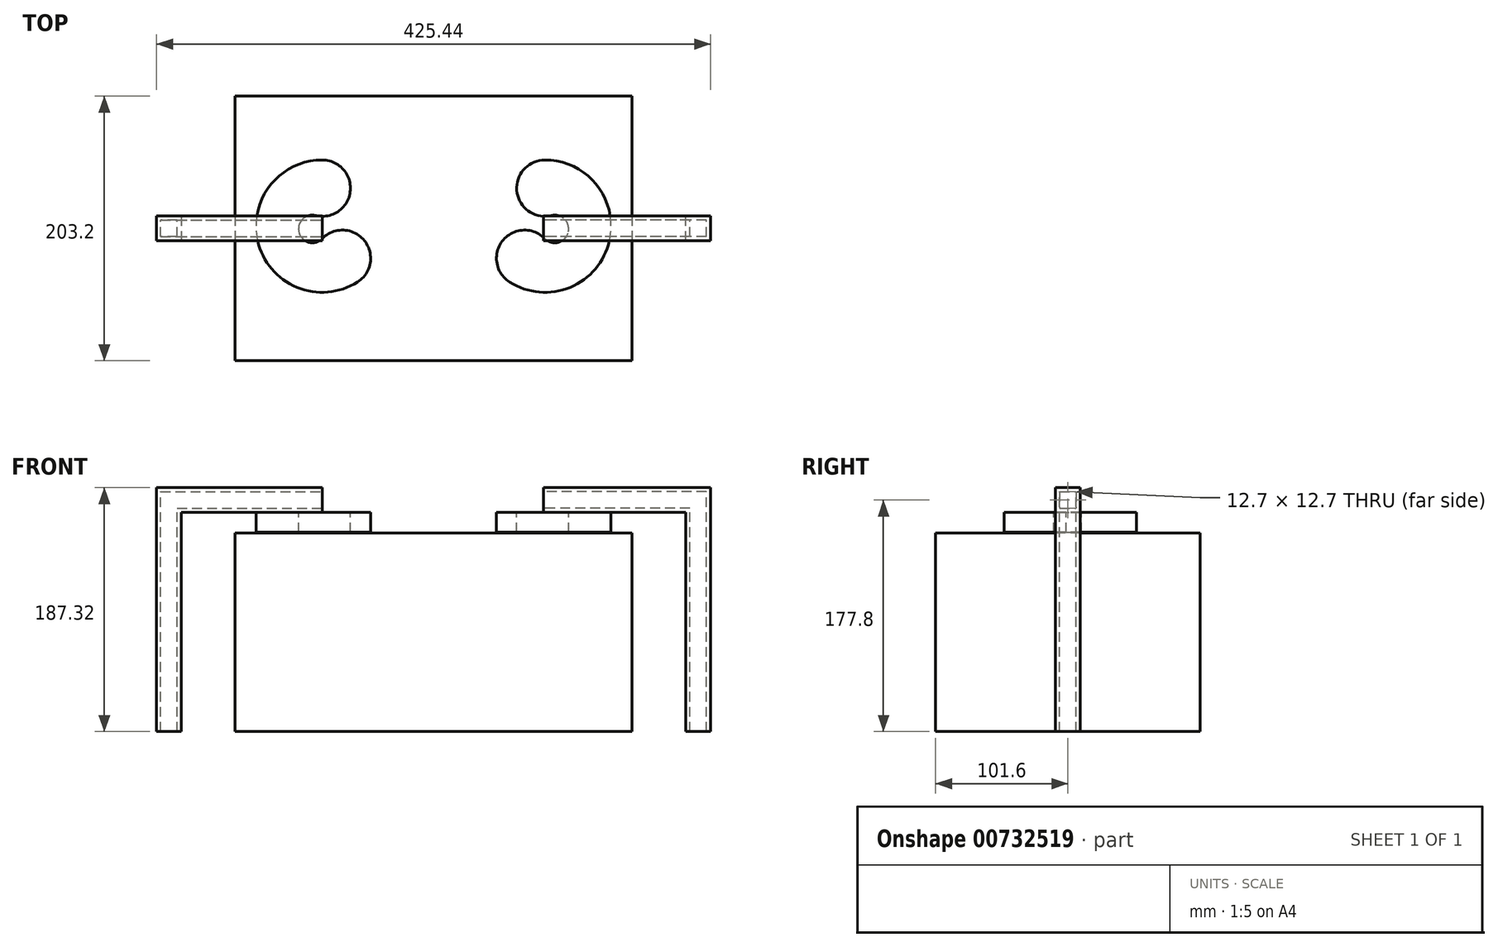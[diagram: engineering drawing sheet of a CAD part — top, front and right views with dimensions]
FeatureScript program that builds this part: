
annotation { "Feature Type Name" : "Feature", "Feature Type Description" : "" }
export const myFeature = defineFeature(function(context is Context, id is Id, definition is map)
    precondition{}
    {
        {
            var Q0;
            Q0=qCreatedBy(makeId("Front.planeOp"),FACE);
            var sketch = newSketch(context, id + "F0", { "sketchPlane" : qUnion([Q0])});
            skLineSegment(sketch, "E0.bottom", {"start": v(-152.4, 0) * mm, "end": v(152.4, 0) * mm});
            skLineSegment(sketch, "E0.top", {"start": v(-152.4, 152.4) * mm, "end": v(152.4, 152.4) * mm});
            skLineSegment(sketch, "E0.left", {"start": v(-152.4, 0) * mm, "end": v(-152.4, 152.4) * mm});
            skLineSegment(sketch, "E0.right", {"start": v(152.4, 0) * mm, "end": v(152.4, 152.4) * mm});
            skSolve(sketch);
        }
        {
            var Q0;
            Q0 = qSketchRegion(id + "F0", true);
            extrude(context, id + "F1", {"entities" : qUnion([Q0]), "oppositeDirection" : true, "depth" : 203.2 * mm, "offsetDistance" : 25.4 * mm});
        }
        {
            var Q0;
            Q0=qCreatedBy(makeId("Front.planeOp"),FACE);
            cPlane(context, id + "F2", {"entities" : qUnion([Q0]), "cplaneType" : CPlaneType.OFFSET, "offset" : 101.6 * mm, "oppositeDirection" : true, "width" : 152.4 * mm, "height" : 152.4 * mm});
        }
        {
            var Q0;
            Q0=qCreatedBy(id+"F2.planeOp",FACE);
            var sketch = newSketch(context, id + "F3", { "sketchPlane" : qUnion([Q0])});
            skLineSegment(sketch, "E1", {"start": v(-203.2, 0) * mm, "end": v(-203.2, 177.8) * mm});
            skLineSegment(sketch, "E2", {"start": v(-203.2, 177.8) * mm, "end": v(-85.5, 177.8) * mm});
            skLineSegment(sketch, "E3", {"start": v(203.2, 0) * mm, "end": v(203.2, 177.8) * mm});
            skLineSegment(sketch, "E4", {"start": v(203.2, 177.8) * mm, "end": v(84.39, 177.8) * mm});
            skSolve(sketch);
        }
        {
            var Q0;
            Q0=qCreatedBy(makeId("Top.planeOp"),FACE);
            var sketch = newSketch(context, id + "F4", { "sketchPlane" : qUnion([Q0])});
            skPoint(sketch, "E5.0", {"position": v(-203.2, 101.6) * mm});
            skPoint(sketch, "E6.0", {"position": v(203.2, 101.6) * mm});
            skLineSegment(sketch, "E7.bottom", {"start": v(-193.68, 92.07) * mm, "end": v(-212.73, 92.07) * mm});
            skLineSegment(sketch, "E7.top", {"start": v(-193.68, 111.12) * mm, "end": v(-212.73, 111.12) * mm});
            skLineSegment(sketch, "E7.left", {"start": v(-193.68, 92.07) * mm, "end": v(-193.68, 111.12) * mm});
            skLineSegment(sketch, "E7.right", {"start": v(-212.73, 92.07) * mm, "end": v(-212.73, 111.12) * mm});
            skLineSegment(sketch, "E8.bottom", {"start": v(-196.85, 95.25) * mm, "end": v(-209.55, 95.25) * mm});
            skLineSegment(sketch, "E8.top", {"start": v(-196.85, 107.95) * mm, "end": v(-209.55, 107.95) * mm});
            skLineSegment(sketch, "E8.left", {"start": v(-196.85, 95.25) * mm, "end": v(-196.85, 107.95) * mm});
            skLineSegment(sketch, "E8.right", {"start": v(-209.55, 95.25) * mm, "end": v(-209.55, 107.95) * mm});
            skLineSegment(sketch, "E9.bottom", {"start": v(212.73, 92.08) * mm, "end": v(193.68, 92.08) * mm});
            skLineSegment(sketch, "E9.top", {"start": v(212.73, 111.13) * mm, "end": v(193.68, 111.13) * mm});
            skLineSegment(sketch, "E9.left", {"start": v(212.73, 92.08) * mm, "end": v(212.73, 111.13) * mm});
            skLineSegment(sketch, "E9.right", {"start": v(193.68, 92.08) * mm, "end": v(193.68, 111.13) * mm});
            skLineSegment(sketch, "E10.bottom", {"start": v(209.55, 95.25) * mm, "end": v(196.85, 95.25) * mm});
            skLineSegment(sketch, "E10.top", {"start": v(209.55, 107.95) * mm, "end": v(196.85, 107.95) * mm});
            skLineSegment(sketch, "E10.left", {"start": v(209.55, 95.25) * mm, "end": v(209.55, 107.95) * mm});
            skLineSegment(sketch, "E10.right", {"start": v(196.85, 95.25) * mm, "end": v(196.85, 107.95) * mm});
            skSolve(sketch);
        }
        {
            var Q0;
            Q0=makeQuery(id+"F4.imprint","IMPRINT",FACE,{"disambiguationData":[TD([[makeQuery(id+"F4.imprint","IMPRINT",EDGE,{"derivedFrom":sQuery(id+"F4.wireOp",EDGE,"E9.bottom")}),-1.0]])]});
            var Q1;
            Q1=sQuery(id+"F3.wireOp",EDGE,"E3");
            var Q2;
            Q2=sQuery(id+"F3.wireOp",EDGE,"E4");
            sweep(context, id + "F5", {"profiles" : qUnion([Q0]), "path" : qUnion([Q1, Q2])});
        }
        {
            var Q0;
            Q0=makeQuery(id+"F4.imprint","IMPRINT",FACE,{"disambiguationData":[TD([[makeQuery(id+"F4.imprint","IMPRINT",EDGE,{"derivedFrom":sQuery(id+"F4.wireOp",EDGE,"E7.bottom")}),-1.0]])]});
            var Q1;
            Q1=sQuery(id+"F3.wireOp",EDGE,"E1");
            var Q2;
            Q2=sQuery(id+"F3.wireOp",EDGE,"E2");
            sweep(context, id + "F6", {"profiles" : qUnion([Q0]), "path" : qUnion([Q1, Q2])});
        }
        {
            var Q0;
            Q0=makeQuery(id+"F6.opSweep","SWEPT_FACE",FACE,{"disambiguationData":[OSD([sQuery(id+"F3.wireOp",EDGE,"E2"),sQuery(id+"F4.wireOp",EDGE,"E7.left")])]});
            var sketch = newSketch(context, id + "F7", { "sketchPlane" : qUnion([Q0])});
            skArc(sketch, "E11", {"start": v(-85.47, -154.21) * mm, "mid": v(-134.3, -89.36) * mm, "end": v(-58.46, -60.4) * mm});
            skArc(sketch, "E12", {"start": v(-85.47, -93.81) * mm, "mid": v(-53.14, -92.32) * mm, "end": v(-58.46, -60.4) * mm});
            skArc(sketch, "E13", {"start": v(-85.47, -154.21) * mm, "mid": v(-63.99, -130) * mm, "end": v(-90.58, -111.54) * mm});
            skArc(sketch, "E14", {"start": v(-85.47, -93.81) * mm, "mid": v(-103.3, -98.28) * mm, "end": v(-90.58, -111.54) * mm});
            skLineSegment(sketch, "E15", {"start": v(0, 0) * mm, "end": v(0, -204.95) * mm, "construction": true});
            skArc(sketch, "E16.MirrorCS", {"start": v(85.47, -93.81) * mm, "mid": v(53.14, -92.32) * mm, "end": v(58.46, -60.4) * mm});
            skArc(sketch, "E17.MirrorCS", {"start": v(85.47, -154.21) * mm, "mid": v(134.3, -89.36) * mm, "end": v(58.46, -60.4) * mm});
            skArc(sketch, "E18.MirrorCS", {"start": v(85.47, -93.81) * mm, "mid": v(103.3, -98.28) * mm, "end": v(90.58, -111.54) * mm});
            skArc(sketch, "E19.MirrorCS", {"start": v(85.47, -154.21) * mm, "mid": v(63.99, -130) * mm, "end": v(90.58, -111.54) * mm});
            skSolve(sketch);
        }
        {
            var Q0;
            Q0 = qSketchRegion(id + "F7", true);
            extrude(context, id + "F8", {"entities" : qUnion([Q0]), "operationType" : NewBodyOperationType.ADD, "depth" : 15.24 * mm, "offsetDistance" : 25.4 * mm});
        }
    });
